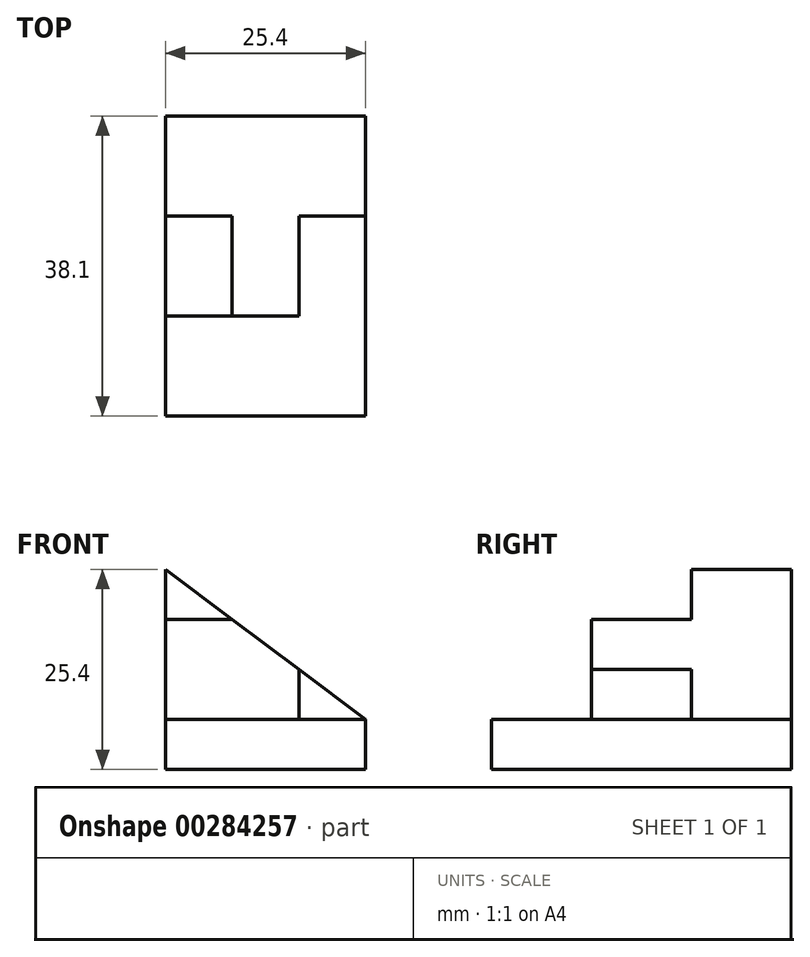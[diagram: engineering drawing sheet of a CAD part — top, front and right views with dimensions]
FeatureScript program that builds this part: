
annotation { "Feature Type Name" : "Feature", "Feature Type Description" : "" }
export const myFeature = defineFeature(function(context is Context, id is Id, definition is map)
    precondition{}
    {
        {
            var Q0;
            Q0=qCreatedBy(makeId("Front.planeOp"),FACE);
            var sketch = newSketch(context, id + "F0", { "sketchPlane" : qUnion([Q0])});
            skLineSegment(sketch, "E0", {"start": v(0, 0) * mm, "end": v(25.4, 0) * mm});
            skLineSegment(sketch, "E1", {"start": v(25.4, 0) * mm, "end": v(25.4, 6.35) * mm});
            skLineSegment(sketch, "E2", {"start": v(25.4, 6.35) * mm, "end": v(0, 6.35) * mm});
            skLineSegment(sketch, "E3", {"start": v(0, 6.35) * mm, "end": v(0, 0) * mm});
            skLineSegment(sketch, "E4", {"start": v(0, 6.35) * mm, "end": v(0, 25.4) * mm});
            skLineSegment(sketch, "E5", {"start": v(0, 25.4) * mm, "end": v(25.4, 6.35) * mm});
            skLineSegment(sketch, "E6", {"start": v(0, 19.05) * mm, "end": v(8.47, 19.05) * mm});
            skLineSegment(sketch, "E7", {"start": v(17.78, 12.07) * mm, "end": v(17.78, 6.35) * mm});
            skSolve(sketch);
        }
        {
            var Q0;
            Q0=makeQuery(id+"F0.imprint","IMPRINT",FACE,{"disambiguationData":[TD([[makeQuery(id+"F0.imprint","IMPRINT",EDGE,{"derivedFrom":sQuery(id+"F0.wireOp",EDGE,"E0")}),1.0]])]});
            var Q1;
            {var subQ3=sQuery(id+"F0.wireOp",EDGE,"E7");Q1=makeQuery(id+"F0.imprint","IMPRINT",FACE,{"disambiguationData":[TD([[makeQuery(id+"F0.imprint","IMPRINT",EDGE,{"derivedFrom":subQ3}),1.0]])]});}
            var Q2;
            {var subQ0=sQuery(id+"F0.wireOp",EDGE,"E6");Q2=makeQuery(id+"F0.imprint","IMPRINT",FACE,{"disambiguationData":[TD([[makeQuery(id+"F0.imprint","IMPRINT",EDGE,{"derivedFrom":subQ0}),-1.0]])]});}
            var Q3;
            {var subQ3=sQuery(id+"F0.wireOp",EDGE,"E6");Q3=makeQuery(id+"F0.imprint","IMPRINT",FACE,{"disambiguationData":[TD([[makeQuery(id+"F0.imprint","IMPRINT",EDGE,{"derivedFrom":subQ3}),1.0]])]});}
            extrude(context, id + "F1", {"entities" : qUnion([Q0, Q1, Q2, Q3]), "depth" : 38.1 * mm});
        }
        {
            var Q0;
            Q0=makeQuery(id+"F1.opExtrude","CAP_FACE",FACE,{"disambiguationData":[OSD([sQuery(id+"F0.wireOp",EDGE,"E0"),sQuery(id+"F0.wireOp",EDGE,"E1"),sQuery(id+"F0.wireOp",EDGE,"E3"),sQuery(id+"F0.wireOp",EDGE,"E4"),sQuery(id+"F0.wireOp",EDGE,"E5")])],"isStart":false});
            var sketch = newSketch(context, id + "F2", { "sketchPlane" : qUnion([Q0])});
            skLineSegment(sketch, "E8", {"start": v(25.4, 6.35) * mm, "end": v(0, 6.35) * mm});
            skLineSegment(sketch, "E9", {"start": v(0, 6.35) * mm, "end": v(0, 25.4) * mm});
            skLineSegment(sketch, "E10", {"start": v(0, 25.4) * mm, "end": v(25.4, 6.35) * mm});
            skSolve(sketch);
        }
        {
            var Q0;
            Q0=makeQuery(id+"F2.imprint","IMPRINT",FACE,{"disambiguationData":[TD([[makeQuery(id+"F2.imprint","IMPRINT",EDGE,{"derivedFrom":sQuery(id+"F2.wireOp",EDGE,"E8")}),-1.0]])]});
            extrude(context, id + "F3", {"entities" : qUnion([Q0]), "operationType" : NewBodyOperationType.REMOVE, "oppositeDirection" : true, "depth" : 12.7 * mm});
        }
        {
            var Q0;
            Q0=makeQuery(id+"F3.boolean.opBoolean","COPY",FACE,{"derivedFrom":makeQuery(id+"F3.opExtrude","CAP_FACE",FACE,{"disambiguationData":[OSD([sQuery(id+"F2.wireOp",EDGE,"E8"),sQuery(id+"F2.wireOp",EDGE,"E9"),sQuery(id+"F2.wireOp",EDGE,"E10")])],"isStart":false})});
            var sketch = newSketch(context, id + "F4", { "sketchPlane" : qUnion([Q0])});
            skLineSegment(sketch, "E11", {"start": v(16.93, 6.35) * mm, "end": v(16.93, 12.7) * mm});
            skLineSegment(sketch, "E12", {"start": v(16.93, 12.7) * mm, "end": v(25.4, 6.35) * mm});
            skLineSegment(sketch, "E13", {"start": v(25.4, 6.35) * mm, "end": v(16.93, 6.35) * mm});
            skSolve(sketch);
        }
        {
            var Q0;
            Q0=makeQuery(id+"F4.imprint","IMPRINT",FACE,{"disambiguationData":[TD([[makeQuery(id+"F4.imprint","IMPRINT",EDGE,{"derivedFrom":sQuery(id+"F4.wireOp",EDGE,"E11")}),-1.0]])]});
            extrude(context, id + "F5", {"entities" : qUnion([Q0]), "operationType" : NewBodyOperationType.REMOVE, "oppositeDirection" : true, "depth" : 12.7 * mm});
        }
        {
            var Q0;
            Q0=makeQuery(id+"F3.boolean.opBoolean","COPY",FACE,{"derivedFrom":makeQuery(id+"F3.opExtrude","CAP_FACE",FACE,{"disambiguationData":[OSD([sQuery(id+"F2.wireOp",EDGE,"E8"),sQuery(id+"F2.wireOp",EDGE,"E9"),sQuery(id+"F2.wireOp",EDGE,"E10")])],"isStart":false})});
            var sketch = newSketch(context, id + "F6", { "sketchPlane" : qUnion([Q0])});
            skLineSegment(sketch, "E14", {"start": v(0, 19.05) * mm, "end": v(8.47, 19.05) * mm});
            skLineSegment(sketch, "E15", {"start": v(8.47, 19.05) * mm, "end": v(0, 25.4) * mm});
            skLineSegment(sketch, "E16", {"start": v(0, 25.4) * mm, "end": v(0, 19.05) * mm});
            skSolve(sketch);
        }
        {
            var Q0;
            Q0=makeQuery(id+"F6.imprint","IMPRINT",FACE,{"disambiguationData":[TD([[makeQuery(id+"F6.imprint","IMPRINT",EDGE,{"derivedFrom":sQuery(id+"F6.wireOp",EDGE,"E14")}),1.0]])]});
            extrude(context, id + "F7", {"entities" : qUnion([Q0]), "operationType" : NewBodyOperationType.REMOVE, "oppositeDirection" : true, "depth" : 12.7 * mm});
        }
    });
